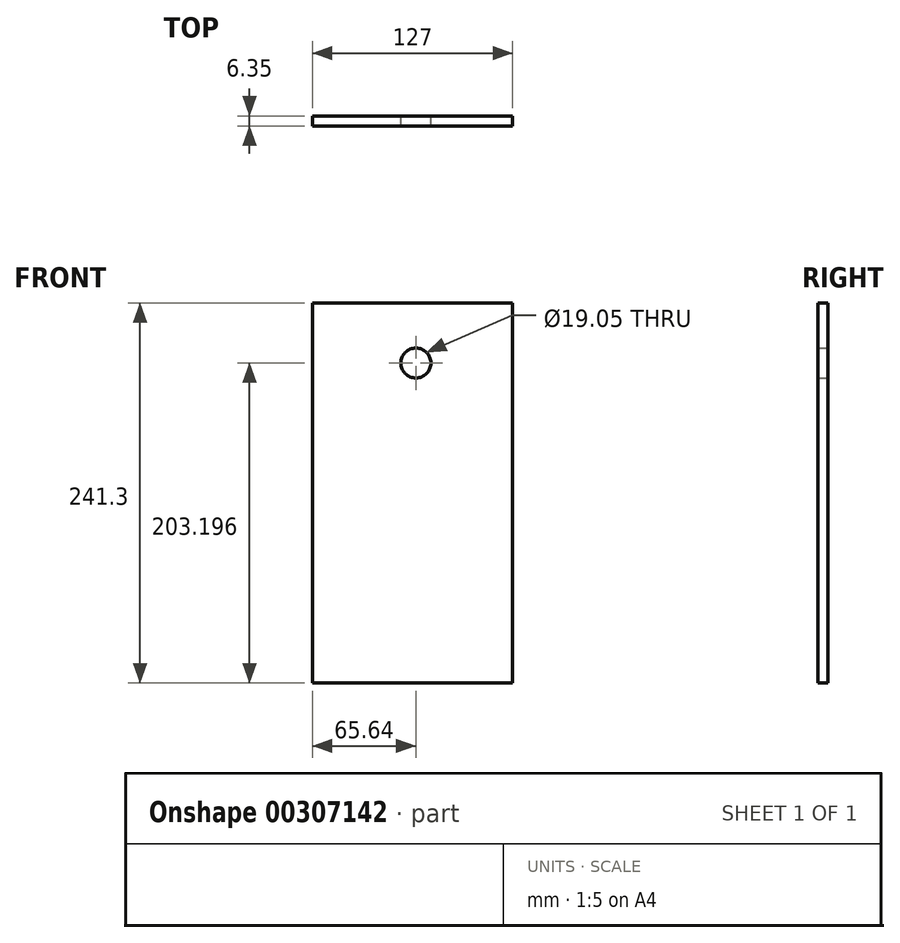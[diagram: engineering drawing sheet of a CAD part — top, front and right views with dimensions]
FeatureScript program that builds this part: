
annotation { "Feature Type Name" : "Feature", "Feature Type Description" : "" }
export const myFeature = defineFeature(function(context is Context, id is Id, definition is map)
    precondition{}
    {
        {
            var Q0;
            Q0=qCreatedBy(makeId("Front.planeOp"),FACE);
            var sketch = newSketch(context, id + "F0", { "sketchPlane" : qUnion([Q0])});
            skLineSegment(sketch, "E0.bottom", {"start": v(-100.44, 116.63) * mm, "end": v(26.56, 116.63) * mm});
            skLineSegment(sketch, "E0.top", {"start": v(-100.44, -124.67) * mm, "end": v(26.56, -124.67) * mm});
            skLineSegment(sketch, "E0.left", {"start": v(-100.44, 116.63) * mm, "end": v(-100.44, -124.67) * mm});
            skLineSegment(sketch, "E0.right", {"start": v(26.56, 116.63) * mm, "end": v(26.56, -124.67) * mm});
            skCircle(sketch, "E1", {"center": v(-34.8, 78.53) * mm, "radius": 9.53 * mm});
            skSolve(sketch);
        }
        {
            var Q0;
            Q0 = qSketchRegion(id + "F0", true);
            extrude(context, id + "F1", {"entities" : qUnion([Q0]), "depth" : 6.35 * mm});
        }
    });
